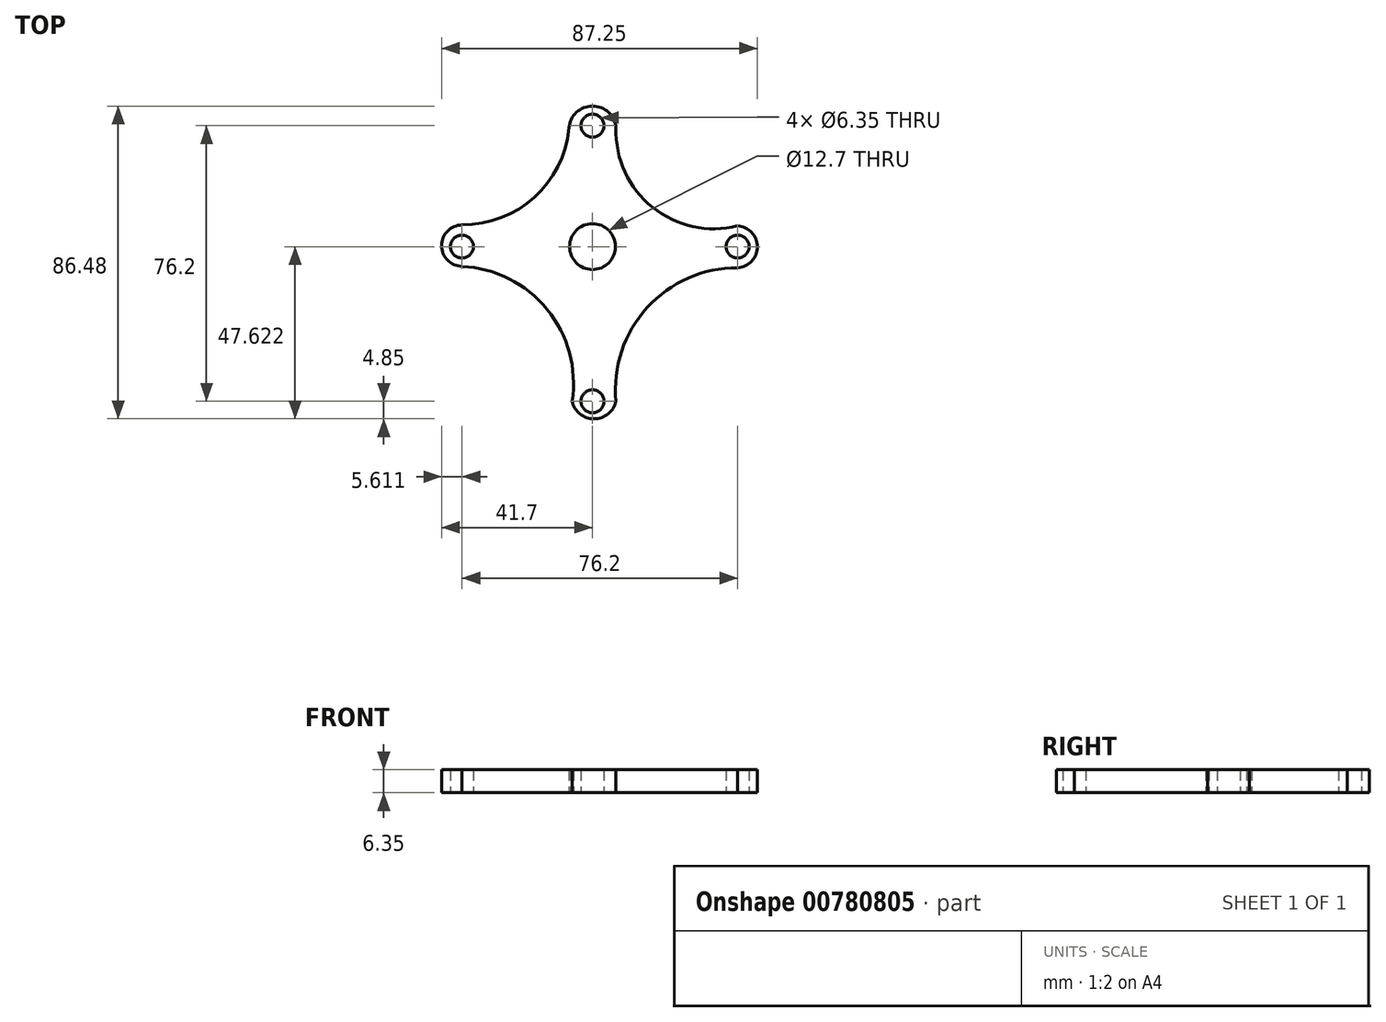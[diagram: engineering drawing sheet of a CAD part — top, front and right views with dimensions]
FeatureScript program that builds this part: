
annotation { "Feature Type Name" : "Feature", "Feature Type Description" : "" }
export const myFeature = defineFeature(function(context is Context, id is Id, definition is map)
    precondition{}
    {
        {
            var Q0;
            Q0=qCreatedBy(makeId("Top.planeOp"),FACE);
            var sketch = newSketch(context, id + "F0", { "sketchPlane" : qUnion([Q0])});
            skCircle(sketch, "E0", {"center": v(0, 55.47) * mm, "radius": 6.35 * mm});
            skCircle(sketch, "E1", {"center": v(0, 88.9) * mm, "radius": 3.18 * mm});
            skCircle(sketch, "E2", {"center": v(40.11, 55.47) * mm, "radius": 3.18 * mm});
            skCircle(sketch, "E3", {"center": v(0, 12.7) * mm, "radius": 3.18 * mm});
            skCircle(sketch, "E4", {"center": v(-36.09, 55.47) * mm, "radius": 3.18 * mm});
            skArc(sketch, "E5", {"start": v(-36.09, 61.47) * mm, "mid": v(-16.1, 69.1) * mm, "end": v(-6.5, 88.24) * mm});
            skArc(sketch, "E6", {"start": v(-36.09, 61.47) * mm, "mid": v(-41.7, 55.74) * mm, "end": v(-36.09, 50.01) * mm});
            skArc(sketch, "E7", {"start": v(-5.65, 12.7) * mm, "mid": v(-12.56, 38.14) * mm, "end": v(-36.09, 50.01) * mm});
            skArc(sketch, "E8", {"start": v(6.5, 88.24) * mm, "mid": v(0, 94.33) * mm, "end": v(-6.5, 88.24) * mm});
            skArc(sketch, "E9", {"start": v(6.5, 88.24) * mm, "mid": v(16.58, 66.36) * mm, "end": v(40.11, 61.2) * mm});
            skArc(sketch, "E10", {"start": v(40.11, 49.61) * mm, "mid": v(45.55, 55.4) * mm, "end": v(40.11, 61.2) * mm});
            skArc(sketch, "E11", {"start": v(40.11, 49.61) * mm, "mid": v(15.12, 38.6) * mm, "end": v(6.5, 12.7) * mm});
            skArc(sketch, "E12", {"start": v(-5.65, 12.7) * mm, "mid": v(0.42, 7.85) * mm, "end": v(6.5, 12.7) * mm});
            skPoint(sketch, "E13.top.end.orphan", {"position": v(52.81, 0) * mm});
            skSolve(sketch);
        }
        {
            var Q0;
            Q0 = qSketchRegion(id + "F0", true);
            extrude(context, id + "F1", {"entities" : qUnion([Q0]), "depth" : 6.35 * mm, "offsetDistance" : 25.4 * mm});
        }
    });
